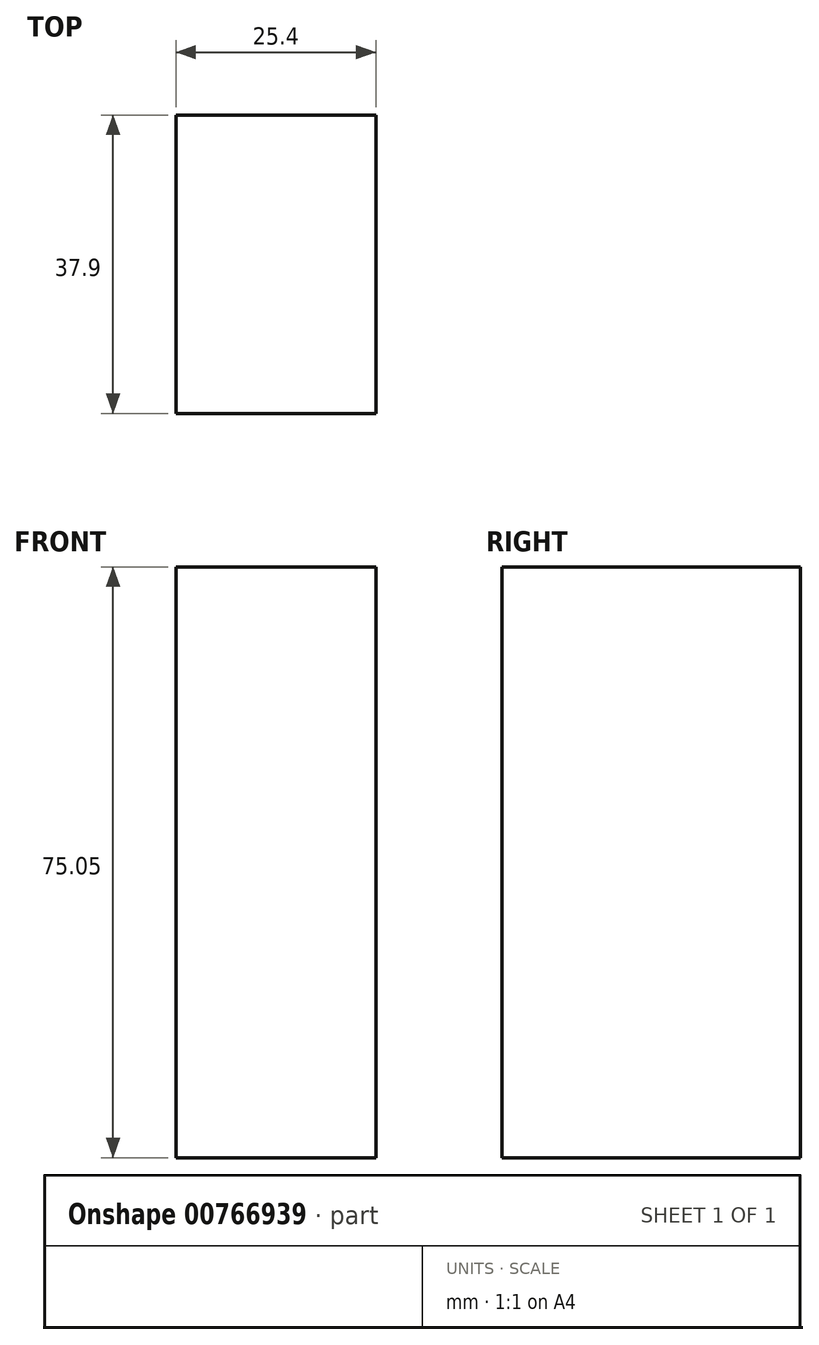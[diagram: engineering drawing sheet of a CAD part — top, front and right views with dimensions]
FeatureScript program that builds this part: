
annotation { "Feature Type Name" : "Feature", "Feature Type Description" : "" }
export const myFeature = defineFeature(function(context is Context, id is Id, definition is map)
    precondition{}
    {
        {
            var Q0;
            Q0=qCreatedBy(makeId("Right.planeOp"),FACE);
            var sketch = newSketch(context, id + "F0", { "sketchPlane" : qUnion([Q0])});
            skLineSegment(sketch, "E0.bottom", {"start": v(-18.05, 0) * mm, "end": v(19.85, 0) * mm});
            skLineSegment(sketch, "E0.top", {"start": v(-18.05, -75.05) * mm, "end": v(19.85, -75.05) * mm});
            skLineSegment(sketch, "E0.left", {"start": v(-18.05, 0) * mm, "end": v(-18.05, -75.05) * mm});
            skLineSegment(sketch, "E0.right", {"start": v(19.85, 0) * mm, "end": v(19.85, -75.05) * mm});
            skSolve(sketch);
        }
        {
            var Q0;
            Q0 = qSketchRegion(id + "F0", true);
            extrude(context, id + "F1", {"entities" : qUnion([Q0]), "depth" : 25.4 * mm, "offsetDistance" : 25.4 * mm});
        }
    });
